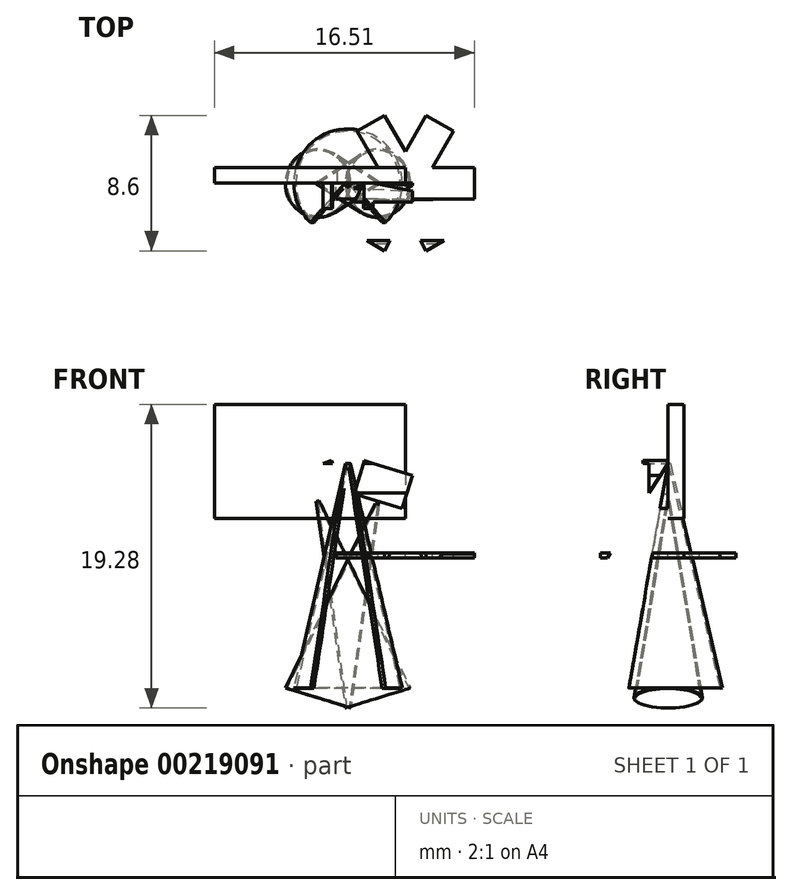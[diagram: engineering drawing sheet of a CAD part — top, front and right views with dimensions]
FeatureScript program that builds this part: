
annotation { "Feature Type Name" : "Feature", "Feature Type Description" : "" }
export const myFeature = defineFeature(function(context is Context, id is Id, definition is map)
    precondition{}
    {
        {
            var Q0;
            Q0=qCreatedBy(makeId("Top.planeOp"),FACE);
            var sketch = newSketch(context, id + "F0", { "sketchPlane" : qUnion([Q0])});
            skCircle(sketch, "E0.cCircle", {"center": v(0, 0) * mm, "radius": 2 * mm, "construction": true});
            skLineSegment(sketch, "E0.0", {"start": v(-2, 0) * mm, "end": v(-1.73, 1) * mm, "construction": true});
            skLineSegment(sketch, "E0.1", {"start": v(-1.73, 1) * mm, "end": v(-1, 1.73) * mm, "construction": true});
            skLineSegment(sketch, "E0.2", {"start": v(-1, 1.73) * mm, "end": v(0, 2) * mm, "construction": true});
            skLineSegment(sketch, "E0.3", {"start": v(0, 2) * mm, "end": v(1, 1.73) * mm, "construction": true});
            skLineSegment(sketch, "E0.4", {"start": v(1, 1.73) * mm, "end": v(1.73, 1) * mm, "construction": true});
            skLineSegment(sketch, "E0.5", {"start": v(1.73, 1) * mm, "end": v(2, 0) * mm, "construction": true});
            skLineSegment(sketch, "E0.6", {"start": v(2, 0) * mm, "end": v(1.73, -1) * mm, "construction": true});
            skLineSegment(sketch, "E0.7", {"start": v(1.73, -1) * mm, "end": v(1, -1.73) * mm, "construction": true});
            skLineSegment(sketch, "E0.8", {"start": v(1, -1.73) * mm, "end": v(0, -2) * mm, "construction": true});
            skLineSegment(sketch, "E0.9", {"start": v(0, -2) * mm, "end": v(-1, -1.73) * mm, "construction": true});
            skLineSegment(sketch, "E0.10", {"start": v(-1, -1.73) * mm, "end": v(-1.73, -1) * mm, "construction": true});
            skLineSegment(sketch, "E0.11", {"start": v(-1.73, -1) * mm, "end": v(-2, 0) * mm, "construction": true});
            skCircle(sketch, "E1", {"center": v(0, 0) * mm, "radius": 4.5 * mm, "construction": true});
            skLineSegment(sketch, "E2", {"start": v(-1.73, 1) * mm, "end": v(-4.3, 1) * mm});
            skLineSegment(sketch, "E3", {"start": v(-1.73, -1) * mm, "end": v(-4.39, -1) * mm});
            skLineSegment(sketch, "E4", {"start": v(0, 0) * mm, "end": v(-1, 1.73) * mm, "construction": true});
            skLineSegment(sketch, "E5", {"start": v(0, 0) * mm, "end": v(1, 1.73) * mm, "construction": true});
            skLineSegment(sketch, "E6", {"start": v(-1.73, 1) * mm, "end": v(-3.06, 3.3) * mm});
            skLineSegment(sketch, "E7", {"start": v(0, 2) * mm, "end": v(-1.33, 4.3) * mm});
            skLineSegment(sketch, "E8", {"start": v(0, 2) * mm, "end": v(1.33, 4.3) * mm});
            skLineSegment(sketch, "E9", {"start": v(1.73, 1) * mm, "end": v(3.06, 3.3) * mm});
            skLineSegment(sketch, "E10", {"start": v(-1.73, -1) * mm, "end": v(0, 0) * mm, "construction": true});
            skLineSegment(sketch, "E11", {"start": v(-4.39, -1) * mm, "end": v(-4.39, 0) * mm});
            skLineSegment(sketch, "E12", {"start": v(-3.06, 3.3) * mm, "end": v(-1.33, 4.3) * mm});
            skLineSegment(sketch, "E13", {"start": v(1.33, 4.3) * mm, "end": v(3.06, 3.3) * mm});
            skLineSegment(sketch, "E14.MirrorCS", {"start": v(-1.73, -1) * mm, "end": v(-3.06, -3.3) * mm});
            skLineSegment(sketch, "E15.MirrorCS", {"start": v(-3.06, -3.3) * mm, "end": v(-1.33, -4.3) * mm});
            skLineSegment(sketch, "E16.MirrorCS", {"start": v(0, -2) * mm, "end": v(-1.33, -4.3) * mm});
            skLineSegment(sketch, "E17.MirrorCS", {"start": v(0, -2) * mm, "end": v(1.33, -4.3) * mm});
            skLineSegment(sketch, "E18.MirrorCS", {"start": v(1.33, -4.3) * mm, "end": v(3.06, -3.3) * mm});
            skLineSegment(sketch, "E19.MirrorCS", {"start": v(1.73, -1) * mm, "end": v(3.06, -3.3) * mm});
            skLineSegment(sketch, "E20.MirrorCS", {"start": v(1.73, -1) * mm, "end": v(4.39, -1) * mm});
            skLineSegment(sketch, "E21.MirrorCS", {"start": v(4.39, -1) * mm, "end": v(4.39, 1) * mm});
            skLineSegment(sketch, "E22.MirrorCS", {"start": v(1.73, 1) * mm, "end": v(4.39, 1) * mm});
            skLineSegment(sketch, "E23", {"start": v(-4.39, 0) * mm, "end": v(-4.3, 0) * mm});
            skLineSegment(sketch, "E24", {"start": v(-4.3, 0) * mm, "end": v(-4.3, 1) * mm});
            skPoint(sketch, "E25.orphan", {"position": v(-4.39, 1) * mm});
            skSolve(sketch);
        }
        {
            var Q0;
            Q0=qCreatedBy(makeId("Front.planeOp"),FACE);
            var sketch = newSketch(context, id + "F1", { "sketchPlane" : qUnion([Q0])});
            skLineSegment(sketch, "E26", {"start": v(0, 0) * mm, "end": v(0, 2) * mm});
            skLineSegment(sketch, "E27", {"start": v(0, 0) * mm, "end": v(0, -8.6) * mm});
            skLineSegment(sketch, "E28", {"start": v(-6.85, 2.2) * mm, "end": v(0.47, 2.2) * mm, "construction": true});
            skLineSegment(sketch, "E29", {"start": v(-4.39, 0) * mm, "end": v(-3.64, 0) * mm, "construction": true});
            skLineSegment(sketch, "E30.bottom", {"start": v(-2.04, 5.7) * mm, "end": v(-5.24, 5.7) * mm});
            skLineSegment(sketch, "E30.top", {"start": v(-2.04, 7.9) * mm, "end": v(-5.24, 7.9) * mm});
            skLineSegment(sketch, "E30.left", {"start": v(-2.04, 5.7) * mm, "end": v(-2.04, 7.9) * mm});
            skLineSegment(sketch, "E30.right", {"start": v(-5.24, 5.7) * mm, "end": v(-5.24, 7.9) * mm});
            skPoint(sketch, "E30.middle", {"position": v(-3.64, 6.8) * mm});
            skLineSegment(sketch, "E31", {"start": v(-3.64, 5.7) * mm, "end": v(-0.34, -8.6) * mm, "construction": true});
            skLineSegment(sketch, "E32", {"start": v(-3.64, 5.7) * mm, "end": v(-6.94, -8.6) * mm});
            skLineSegment(sketch, "E33", {"start": v(-6.94, -8.6) * mm, "end": v(-0.34, -8.6) * mm, "construction": true});
            skPoint(sketch, "E34", {"position": v(-3.64, -8.6) * mm});
            skLineSegment(sketch, "E35", {"start": v(-4.03, 3.76) * mm, "end": v(-7.1, 2.83) * mm});
            skLineSegment(sketch, "E36", {"start": v(-7.1, 2.83) * mm, "end": v(-7.74, 4.93) * mm});
            skLineSegment(sketch, "E37", {"start": v(-7.74, 4.93) * mm, "end": v(-4.68, 5.87) * mm});
            skLineSegment(sketch, "E38", {"start": v(-4.68, 5.87) * mm, "end": v(-4.03, 3.76) * mm});
            skLineSegment(sketch, "E39", {"start": v(-7.1, 2.83) * mm, "end": v(-4.68, 5.87) * mm, "construction": true});
            skLineSegment(sketch, "E40", {"start": v(-4.03, 3.76) * mm, "end": v(-7.74, 4.93) * mm, "construction": true});
            skPoint(sketch, "E41", {"position": v(-5.88, 4.35) * mm});
            skLineSegment(sketch, "E42", {"start": v(-5.56, 3.3) * mm, "end": v(-3.72, -9.81) * mm});
            skLineSegment(sketch, "E43", {"start": v(-3.72, -9.81) * mm, "end": v(0.24, -8.6) * mm, "construction": true});
            skLineSegment(sketch, "E44", {"start": v(0.24, -8.6) * mm, "end": v(-5.56, 3.3) * mm, "construction": true});
            skLineSegment(sketch, "E45", {"start": v(-5.88, 4.35) * mm, "end": v(-5.56, 3.3) * mm, "construction": true});
            skPoint(sketch, "E46", {"position": v(-1.74, -9.2) * mm});
            skPoint(sketch, "E47", {"position": v(-3.64, 5.7) * mm});
            skLineSegment(sketch, "E48", {"start": v(-5.56, 3.3) * mm, "end": v(-5.47, 3) * mm, "construction": true});
            skLineSegment(sketch, "E49", {"start": v(-3.64, 5.7) * mm, "end": v(-3.64, 5.39) * mm, "construction": true});
            skLineSegment(sketch, "E50.0", {"start": v(-5.66, 3.27) * mm, "end": v(-3.82, -9.84) * mm});
            skLineSegment(sketch, "E51", {"start": v(-3.82, -9.84) * mm, "end": v(-3.72, -9.81) * mm});
            skLineSegment(sketch, "E52.0", {"start": v(-3.8, 5.7) * mm, "end": v(-7.09, -8.57) * mm});
            skLineSegment(sketch, "E53", {"start": v(-3.8, 5.7) * mm, "end": v(-3.65, 5.67) * mm});
            skLineSegment(sketch, "E54", {"start": v(-7.09, -8.57) * mm, "end": v(-6.94, -8.6) * mm});
            skLineSegment(sketch, "E55.bottom", {"start": v(-0.2, 2.83) * mm, "end": v(-3.26, 3.76) * mm});
            skLineSegment(sketch, "E55.top", {"start": v(0.45, 4.93) * mm, "end": v(-2.61, 5.87) * mm});
            skLineSegment(sketch, "E55.left", {"start": v(-0.2, 2.83) * mm, "end": v(0.45, 4.93) * mm});
            skLineSegment(sketch, "E55.right", {"start": v(-3.26, 3.76) * mm, "end": v(-2.61, 5.87) * mm});
            skPoint(sketch, "E55.middle", {"position": v(-1.4, 4.35) * mm});
            skLineSegment(sketch, "E56", {"start": v(-1.73, 3.3) * mm, "end": v(-1.82, 3) * mm, "construction": true});
            skLineSegment(sketch, "E57", {"start": v(-1.73, 3.3) * mm, "end": v(-3.57, -9.81) * mm, "construction": true});
            skLineSegment(sketch, "E58", {"start": v(-1.73, 3.3) * mm, "end": v(-7.53, -8.6) * mm});
            skLineSegment(sketch, "E59", {"start": v(-7.53, -8.6) * mm, "end": v(-3.57, -9.81) * mm, "construction": true});
            skPoint(sketch, "E60", {"position": v(-5.55, -9.2) * mm});
            skLineSegment(sketch, "E61.0", {"start": v(-1.82, 3.33) * mm, "end": v(-7.62, -8.56) * mm});
            skLineSegment(sketch, "E62", {"start": v(-7.62, -8.56) * mm, "end": v(-7.53, -8.6) * mm});
            skLineSegment(sketch, "E63", {"start": v(-5.88, 4.35) * mm, "end": v(-1.4, 4.35) * mm, "construction": true});
            skPoint(sketch, "E64", {"position": v(-3.65, 4.35) * mm});
            skLineSegment(sketch, "E65", {"start": v(-5.66, 3.27) * mm, "end": v(-5.56, 3.28) * mm});
            skLineSegment(sketch, "E66", {"start": v(-1.82, 3.33) * mm, "end": v(-1.73, 3.28) * mm});
            skLineSegment(sketch, "E67.bottom", {"start": v(-4.57, 5.7) * mm, "end": v(-2.92, 5.7) * mm});
            skLineSegment(sketch, "E67.top", {"start": v(-4.57, 5.39) * mm, "end": v(-2.92, 5.39) * mm});
            skLineSegment(sketch, "E67.left", {"start": v(-4.57, 5.7) * mm, "end": v(-4.57, 5.39) * mm});
            skLineSegment(sketch, "E67.right", {"start": v(-2.92, 5.7) * mm, "end": v(-2.92, 5.39) * mm});
            skLineSegment(sketch, "E68", {"start": v(-4.68, 5.87) * mm, "end": v(-4.3, 4.62) * mm, "construction": true});
            skLineSegment(sketch, "E69", {"start": v(-5.24, 7.9) * mm, "end": v(-5.24, 6.6) * mm});
            skSolve(sketch);
        }
        {
            var Q0;
            {var subQ0=sQuery(id+"F1.wireOp",EDGE,"DM6Nkpt9-bfdF-qlEk-4nzW-YxgicAbqTC96");Q0=makeQuery(id+"F1.imprint","IMPRINT",FACE,{"disambiguationData":[TD([[makeQuery(id+"F1.imprint","IMPRINT",EDGE,{"derivedFrom":subQ0}),-1.0]])]});}
            var Q1;
            {var subQ5=sQuery(id+"F1.wireOp",EDGE,"E51");Q1=makeQuery(id+"F1.imprint","IMPRINT",FACE,{"disambiguationData":[TD([[makeQuery(id+"F1.imprint","IMPRINT",EDGE,{"derivedFrom":subQ5}),1.0]])]});}
            var Q2;
            {var subQ0=sQuery(id+"F1.wireOp",EDGE,"E42");var subQ1=sQuery(id+"F1.wireOp",EDGE,"E32");var subQ2=makeQuery(id+"F1.imprint","INTERSECT",VERTEX,{"derivedFrom":[subQ1,subQ0]});Q2=makeQuery(id+"F1.imprint","IMPRINT",FACE,{"disambiguationData":[TD([[makeQuery(id+"F1.imprint","IMPRINT",EDGE,{"disambiguationData":[TD([[subQ2,-1.0]])],"derivedFrom":subQ1}),-1.0]])]});}
            var Q3;
            {var subQ5=sQuery(id+"F1.wireOp",EDGE,"E42");var subQ7=sQuery(id+"F1.wireOp",EDGE,"E58");var subQ9=makeQuery(id+"F1.imprint","INTERSECT",VERTEX,{"derivedFrom":[subQ5,subQ7]});Q3=makeQuery(id+"F1.imprint","IMPRINT",FACE,{"disambiguationData":[TD([[makeQuery(id+"F1.imprint","IMPRINT",EDGE,{"disambiguationData":[TD([[subQ9,-1.0]])],"derivedFrom":subQ5}),-1.0]])]});}
            var Q4;
            {var subQ0=sQuery(id+"F1.wireOp",EDGE,"E61.0");var subQ1=sQuery(id+"F1.wireOp",EDGE,"E42");var subQ2=makeQuery(id+"F1.imprint","INTERSECT",VERTEX,{"derivedFrom":[subQ1,subQ0]});Q4=makeQuery(id+"F1.imprint","IMPRINT",FACE,{"disambiguationData":[TD([[makeQuery(id+"F1.imprint","IMPRINT",EDGE,{"disambiguationData":[TD([[subQ2,-1.0]])],"derivedFrom":subQ1}),-1.0]])]});}
            var Q5;
            {var subQ0=sQuery(id+"F1.wireOp",EDGE,"E65");Q5=makeQuery(id+"F1.imprint","IMPRINT",FACE,{"disambiguationData":[TD([[makeQuery(id+"F1.imprint","IMPRINT",EDGE,{"derivedFrom":subQ0}),-1.0]])]});}
            var Q6;
            {var subQ0=sQuery(id+"F1.wireOp",EDGE,"E42");var subQ1=sQuery(id+"F1.wireOp",EDGE,"E32");var subQ2=makeQuery(id+"F1.imprint","INTERSECT",VERTEX,{"derivedFrom":[subQ1,subQ0]});Q6=makeQuery(id+"F1.imprint","IMPRINT",FACE,{"disambiguationData":[TD([[makeQuery(id+"F1.imprint","IMPRINT",EDGE,{"disambiguationData":[TD([[subQ2,-1.0]])],"derivedFrom":subQ1}),1.0]])]});}
            var Q7;
            Q7=sQuery(id+"F1.wireOp",EDGE,"E48");
            revolve(context, id + "F2", {"entities" : qUnion([Q0, Q1, Q2, Q3, Q4, Q5, Q6]), "axis" : qUnion([Q7]), "revolveType" : RevolveType.FULL});
        }
        {
            var Q0;
            Q0=makeQuery(id+"F0.imprint","IMPRINT",FACE,{"disambiguationData":[TD([[makeQuery(id+"F0.imprint","IMPRINT",EDGE,{"derivedFrom":sQuery(id+"F0.wireOp",EDGE,"E2")}),1.0]])]});
            extrude(context, id + "F3", {"entities" : qUnion([Q0]), "oppositeDirection" : true, "depth" : 0.3 * mm});
        }
        {
            var Q0;
            Q0=qCreatedBy(makeId("Front.planeOp"),FACE);
            var sketch = newSketch(context, id + "F4", { "sketchPlane" : qUnion([Q0])});
            skLineSegment(sketch, "E70.0", {"start": v(-3.8, 5.7) * mm, "end": v(-7.09, -8.57) * mm});
            skLineSegment(sketch, "E71.0", {"start": v(-7.09, -8.57) * mm, "end": v(-6.94, -8.6) * mm});
            skLineSegment(sketch, "E72.0", {"start": v(-3.65, 5.67) * mm, "end": v(-6.94, -8.6) * mm});
            skLineSegment(sketch, "E73.0", {"start": v(-3.8, 5.7) * mm, "end": v(-3.65, 5.67) * mm});
            skPoint(sketch, "E74.orphan", {"position": v(-3.8, 5.7) * mm});
            skPoint(sketch, "E75.orphan", {"position": v(-3.64, 5.7) * mm});
            skLineSegment(sketch, "E76.0", {"start": v(-3.64, 5.7) * mm, "end": v(-3.64, 5.39) * mm, "construction": true});
            skSolve(sketch);
        }
        {
            var Q0;
            Q0=makeQuery(id+"F4.imprint","IMPRINT",FACE,{"disambiguationData":[TD([[makeQuery(id+"F4.imprint","IMPRINT",EDGE,{"derivedFrom":sQuery(id+"F4.wireOp",EDGE,"E70.0")}),1.0]])]});
            var Q1;
            Q1=sQuery(id+"F4.wireOp",EDGE,"E70.0");
            var Q2;
            Q2=sQuery(id+"F4.wireOp",EDGE,"E76.0");
            revolve(context, id + "F5", {"entities" : qUnion([Q0]), "surfaceEntities" : qUnion([Q1]), "axis" : qUnion([Q2]), "revolveType" : RevolveType.FULL});
        }
        {
            var Q0;
            {var subQ0=sQuery(id+"F1.wireOp",EDGE,"E37");var subQ1=sQuery(id+"F1.wireOp",EDGE,"E30.bottom");var subQ2=makeQuery(id+"F1.imprint","INTERSECT",VERTEX,{"derivedFrom":[subQ1,subQ0]});Q0=makeQuery(id+"F1.imprint","IMPRINT",FACE,{"disambiguationData":[TD([[makeQuery(id+"F1.imprint","IMPRINT",EDGE,{"disambiguationData":[TD([[subQ2,1.0]])],"derivedFrom":subQ1}),-1.0]])]});}
            var Q1;
            {var subQ3=sQuery(id+"F1.wireOp",EDGE,"E55.left");Q1=makeQuery(id+"F1.imprint","IMPRINT",FACE,{"disambiguationData":[TD([[makeQuery(id+"F1.imprint","IMPRINT",EDGE,{"derivedFrom":subQ3}),1.0]])]});}
            var Q2;
            {var subQ0=sQuery(id+"F1.wireOp",EDGE,"E55.top");var subQ1=sQuery(id+"F1.wireOp",EDGE,"E30.bottom");var subQ2=makeQuery(id+"F1.imprint","INTERSECT",VERTEX,{"derivedFrom":[subQ1,subQ0]});Q2=makeQuery(id+"F1.imprint","IMPRINT",FACE,{"disambiguationData":[TD([[makeQuery(id+"F1.imprint","IMPRINT",EDGE,{"disambiguationData":[TD([[subQ2,-1.0]])],"derivedFrom":subQ1}),-1.0]])]});}
            var Q3;
            {var subQ13=sQuery(id+"F1.wireOp",EDGE,"E36");Q3=makeQuery(id+"F1.imprint","IMPRINT",FACE,{"disambiguationData":[TD([[makeQuery(id+"F1.imprint","IMPRINT",EDGE,{"derivedFrom":subQ13}),-1.0]])]});}
            extrude(context, id + "F6", {"entities" : qUnion([Q0, Q1, Q2, Q3]), "depth" : 1.2 * mm});
        }
        {
            var Q0;
            Q0=makeQuery(id+"F1.imprint","IMPRINT",FACE,{"disambiguationData":[TD([[makeQuery(id+"F1.imprint","IMPRINT",EDGE,{"derivedFrom":sQuery(id+"F1.wireOp",EDGE,"E30.top")}),1.0]])]});
            var Q1;
            {var subQ0=sQuery(id+"F1.wireOp",EDGE,"E55.top");var subQ1=sQuery(id+"F1.wireOp",EDGE,"E30.bottom");var subQ2=makeQuery(id+"F1.imprint","INTERSECT",VERTEX,{"derivedFrom":[subQ1,subQ0]});Q1=makeQuery(id+"F1.imprint","IMPRINT",FACE,{"disambiguationData":[TD([[makeQuery(id+"F1.imprint","IMPRINT",EDGE,{"disambiguationData":[TD([[subQ2,-1.0]])],"derivedFrom":subQ1}),-1.0]])]});}
            var Q2;
            {var subQ0=sQuery(id+"F1.wireOp",EDGE,"E37");var subQ1=sQuery(id+"F1.wireOp",EDGE,"E30.bottom");var subQ2=makeQuery(id+"F1.imprint","INTERSECT",VERTEX,{"derivedFrom":[subQ1,subQ0]});Q2=makeQuery(id+"F1.imprint","IMPRINT",FACE,{"disambiguationData":[TD([[makeQuery(id+"F1.imprint","IMPRINT",EDGE,{"disambiguationData":[TD([[subQ2,1.0]])],"derivedFrom":subQ1}),-1.0]])]});}
            extrude(context, id + "F7", {"entities" : qUnion([Q0, Q1, Q2]), "operationType" : NewBodyOperationType.ADD, "depth" : 1.6 * mm});
        }
        {
            var Q0;
            Q0=qCreatedBy(makeId("Front.planeOp"),FACE);
            var sketch = newSketch(context, id + "F8", { "sketchPlane" : qUnion([Q0])});
            skLineSegment(sketch, "E77.bottom", {"start": v(-12.12, 9.44) * mm, "end": v(0, 9.44) * mm});
            skLineSegment(sketch, "E77.top", {"start": v(-12.12, 2.2) * mm, "end": v(0, 2.2) * mm});
            skLineSegment(sketch, "E77.left", {"start": v(-12.12, 9.44) * mm, "end": v(-12.12, 2.2) * mm});
            skLineSegment(sketch, "E77.right", {"start": v(0, 9.44) * mm, "end": v(0, 2.2) * mm});
            skSolve(sketch);
        }
        {
            var Q0;
            Q0=makeQuery(id+"F8.imprint","IMPRINT",FACE,{"disambiguationData":[TD([[makeQuery(id+"F8.imprint","IMPRINT",EDGE,{"derivedFrom":sQuery(id+"F8.wireOp",EDGE,"E77.bottom")}),-1.0]])]});
            extrude(context, id + "F9", {"entities" : qUnion([Q0]), "oppositeDirection" : true, "depth" : 1 * mm});
        }
        {
            var Q0;
            Q0=qCreatedBy(makeId("Front.planeOp"),FACE);
            var sketch = newSketch(context, id + "F10", { "sketchPlane" : qUnion([Q0])});
            skLineSegment(sketch, "E78.0", {"start": v(-1.9, 3.16) * mm, "end": v(-7.62, -8.56) * mm});
            skLineSegment(sketch, "E79.0", {"start": v(-1.82, 3.12) * mm, "end": v(-7.53, -8.6) * mm});
            skPoint(sketch, "E80.0", {"position": v(-7.57, -8.58) * mm});
            skLineSegment(sketch, "E81.0", {"start": v(-1.73, 3.3) * mm, "end": v(-1.82, 3) * mm, "construction": true});
            skLineSegment(sketch, "E82", {"start": v(-1.82, 3.12) * mm, "end": v(-1.9, 3.16) * mm});
            skPoint(sketch, "E83.orphan", {"position": v(-1.73, 3.3) * mm});
            skPoint(sketch, "E84.0.end.orphan", {"position": v(-0.65, 8.21) * mm});
            skPoint(sketch, "E84.0.start.orphan", {"position": v(-0.74, 8.25) * mm});
            skPoint(sketch, "E85.orphan", {"position": v(-1.82, 3.33) * mm});
            skLineSegment(sketch, "E86", {"start": v(-7.62, -8.56) * mm, "end": v(-7.53, -8.6) * mm});
            skSolve(sketch);
        }
        {
            var Q0;
            Q0 = qSketchRegion(id + "F10", true);
            var Q1;
            Q1=sQuery(id+"F10.wireOp",EDGE,"E81.0");
            revolve(context, id + "F11", {"entities" : qUnion([Q0]), "axis" : qUnion([Q1]), "revolveType" : RevolveType.FULL});
        }
        {
            var Q0;
            Q0=qCreatedBy(makeId("Right.planeOp"),FACE);
            var sketch = newSketch(context, id + "F12", { "sketchPlane" : qUnion([Q0])});
            skLineSegment(sketch, "E87", {"start": v(0, 5.7) * mm, "end": v(-2.77, -10.2) * mm});
            skLineSegment(sketch, "E88", {"start": v(-2.77, -10.2) * mm, "end": v(-10.2, -10.2) * mm});
            skLineSegment(sketch, "E89", {"start": v(-10.2, -10.2) * mm, "end": v(0, 5.7) * mm});
            skSolve(sketch);
        }
        {
            var Q0;
            Q0=makeQuery(id+"F12.imprint","IMPRINT",FACE,{"disambiguationData":[TD([[makeQuery(id+"F12.imprint","IMPRINT",EDGE,{"derivedFrom":sQuery(id+"F12.wireOp",EDGE,"E87")}),-1.0]])]});
            extrude(context, id + "F13", {"entities" : qUnion([Q0]), "operationType" : NewBodyOperationType.REMOVE, "oppositeDirection" : true, "depth" : 25 * mm, "symmetric" : true});
        }
    });
